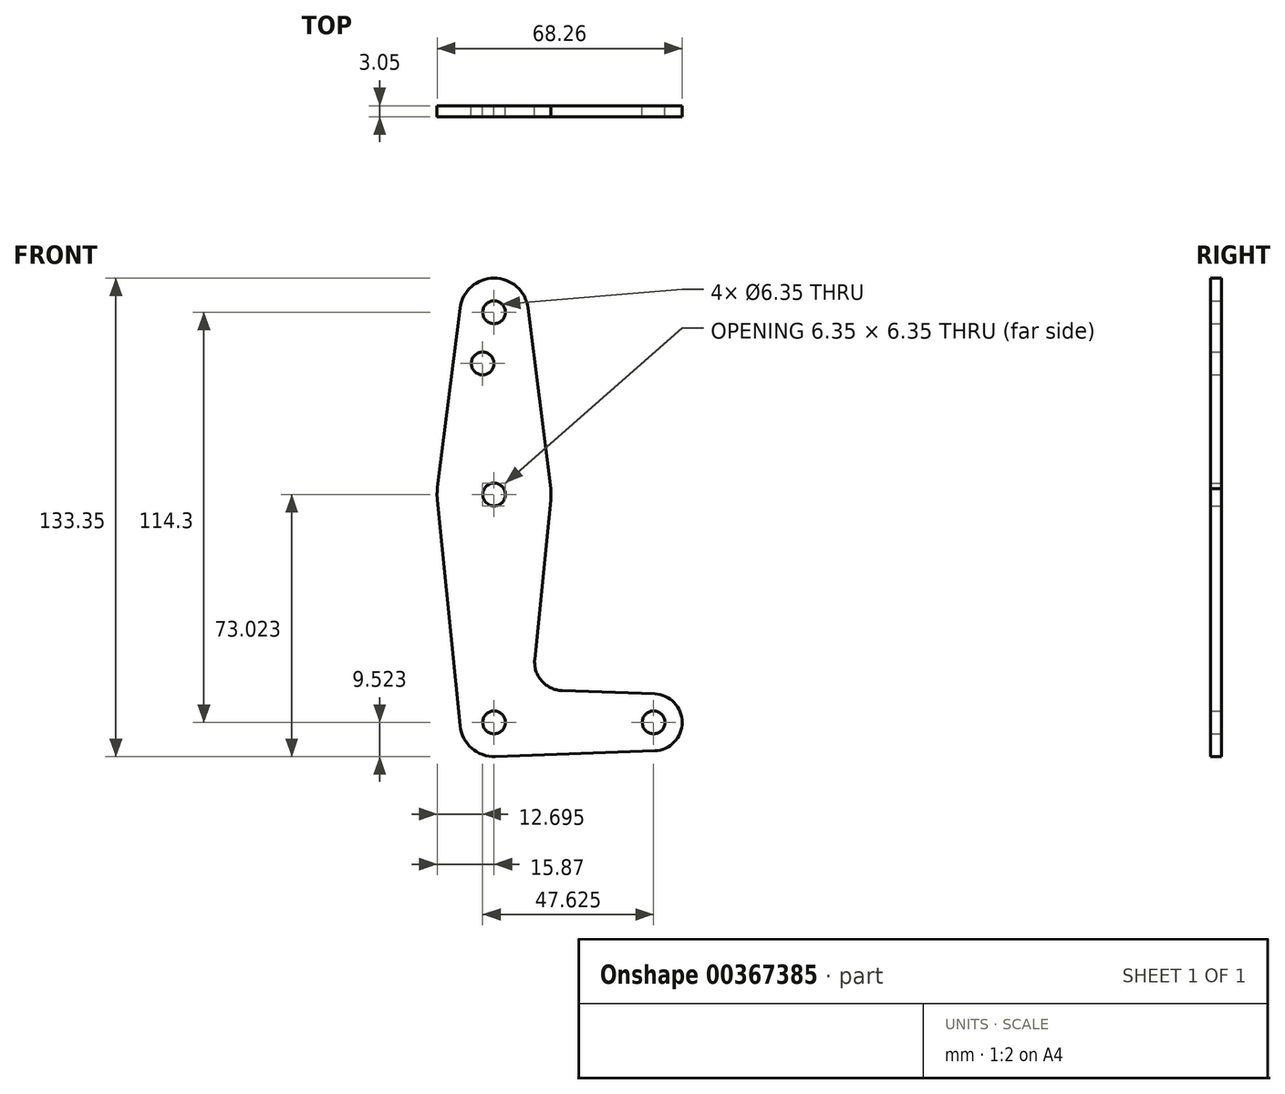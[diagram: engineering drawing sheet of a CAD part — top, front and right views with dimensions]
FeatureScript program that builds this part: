
annotation { "Feature Type Name" : "Feature", "Feature Type Description" : "" }
export const myFeature = defineFeature(function(context is Context, id is Id, definition is map)
    precondition{}
    {
        {
            var Q0;
            Q0=qCreatedBy(makeId("Front.planeOp"),FACE);
            var sketch = newSketch(context, id + "F0", { "sketchPlane" : qUnion([Q0])});
            skLineSegment(sketch, "E0", {"start": v(-44.45, -50.99) * mm, "end": v(-44.45, 63.31) * mm});
            skCircle(sketch, "E1", {"center": v(-44.45, 63.31) * mm, "radius": 9.53 * mm});
            skLineSegment(sketch, "E2", {"start": v(-44.45, -50.99) * mm, "end": v(0, -50.99) * mm});
            skCircle(sketch, "E3", {"center": v(0, -50.99) * mm, "radius": 7.94 * mm});
            skCircle(sketch, "E4", {"center": v(-44.45, -50.99) * mm, "radius": 9.53 * mm});
            skCircle(sketch, "E5", {"center": v(-44.45, 12.51) * mm, "radius": 15.88 * mm});
            skLineSegment(sketch, "E6", {"start": v(-53.9, 64.5) * mm, "end": v(-60.2, 14.5) * mm});
            skLineSegment(sketch, "E7", {"start": v(-53.93, -51.94) * mm, "end": v(-60.25, 10.93) * mm});
            skLineSegment(sketch, "E8", {"start": v(-33.1, -33.4) * mm, "end": v(-28.65, 10.93) * mm});
            skLineSegment(sketch, "E9", {"start": v(-28.65, 14.1) * mm, "end": v(-35, 64.5) * mm});
            skLineSegment(sketch, "E10", {"start": v(-25.48, -42.14) * mm, "end": v(0.28, -43.05) * mm});
            skLineSegment(sketch, "E11", {"start": v(0.28, -43.05) * mm, "end": v(0.28, -58.92) * mm});
            skLineSegment(sketch, "E12", {"start": v(0.28, -58.92) * mm, "end": v(-44.1, -60.5) * mm});
            skCircle(sketch, "E13", {"center": v(-44.45, 63.31) * mm, "radius": 3.18 * mm});
            skCircle(sketch, "E14", {"center": v(-47.62, 49.04) * mm, "radius": 3.18 * mm});
            skCircle(sketch, "E15", {"center": v(-44.45, 12.51) * mm, "radius": 3.18 * mm});
            skCircle(sketch, "E16", {"center": v(-44.45, -50.99) * mm, "radius": 3.18 * mm});
            skCircle(sketch, "E17", {"center": v(0, -50.99) * mm, "radius": 3.18 * mm});
            skArc(sketch, "E18.filletArc", {"start": v(-33.1, -33.4) * mm, "mid": v(-31.19, -39.42) * mm, "end": v(-25.48, -42.14) * mm});
            skSolve(sketch);
        }
        {
            var Q0;
            Q0=makeQuery(id+"F0.imprint","IMPRINT",FACE,{"disambiguationData":[TD([[makeQuery(id+"F0.imprint","IMPRINT",EDGE,{"derivedFrom":sQuery(id+"F0.wireOp",EDGE,"E13")}),-1.0]])]});
            var Q1;
            {var subQ3=sQuery(id+"F0.wireOp",EDGE,"E0");var subQ8=makeQuery(id+"F0.imprint","INTERSECT",VERTEX,{"derivedFrom":[subQ3,sQuery(id+"F0.wireOp",EDGE,"E14")]});Q1=makeQuery(id+"F0.imprint","IMPRINT",FACE,{"disambiguationData":[TD([[makeQuery(id+"F0.imprint","IMPRINT",EDGE,{"disambiguationData":[TD([[subQ8,1.0]])],"derivedFrom":subQ3}),-1.0]])]});}
            var Q2;
            {var subQ0=sQuery(id+"F0.wireOp",EDGE,"E6");Q2=makeQuery(id+"F0.imprint","IMPRINT",FACE,{"disambiguationData":[TD([[makeQuery(id+"F0.imprint","IMPRINT",EDGE,{"derivedFrom":subQ0}),1.0]])]});}
            var Q3;
            {var subQ0=sQuery(id+"F0.wireOp",EDGE,"E5");var subQ2=sQuery(id+"F0.wireOp",EDGE,"E0");var subQ5=makeQuery(id+"F0.imprint","INTERSECT",VERTEX,{"disambiguationData":[OD(0.0)],"derivedFrom":[subQ2,subQ0]});Q3=makeQuery(id+"F0.imprint","IMPRINT",FACE,{"disambiguationData":[TD([[makeQuery(id+"F0.imprint","IMPRINT",EDGE,{"disambiguationData":[TD([[subQ5,-1.0]])],"derivedFrom":subQ2}),1.0]])]});}
            var Q4;
            {var subQ0=sQuery(id+"F0.wireOp",EDGE,"E5");var subQ2=sQuery(id+"F0.wireOp",EDGE,"E0");var subQ3=makeQuery(id+"F0.imprint","INTERSECT",VERTEX,{"disambiguationData":[OD(0.0)],"derivedFrom":[subQ2,subQ0]});Q4=makeQuery(id+"F0.imprint","IMPRINT",FACE,{"disambiguationData":[TD([[makeQuery(id+"F0.imprint","IMPRINT",EDGE,{"disambiguationData":[TD([[subQ3,-1.0]])],"derivedFrom":subQ2}),-1.0]])]});}
            var Q5;
            {var subQ10=sQuery(id+"F0.wireOp",EDGE,"E8");Q5=makeQuery(id+"F0.imprint","IMPRINT",FACE,{"disambiguationData":[TD([[makeQuery(id+"F0.imprint","IMPRINT",EDGE,{"derivedFrom":subQ10}),1.0]])]});}
            var Q6;
            {var subQ5=sQuery(id+"F0.wireOp",EDGE,"E7");Q6=makeQuery(id+"F0.imprint","IMPRINT",FACE,{"disambiguationData":[TD([[makeQuery(id+"F0.imprint","IMPRINT",EDGE,{"derivedFrom":subQ5}),-1.0]])]});}
            var Q7;
            {var subQ5=sQuery(id+"F0.wireOp",EDGE,"E12");Q7=makeQuery(id+"F0.imprint","IMPRINT",FACE,{"disambiguationData":[TD([[makeQuery(id+"F0.imprint","IMPRINT",EDGE,{"derivedFrom":subQ5}),-1.0]])]});}
            var Q8;
            {var subQ3=sQuery(id+"F0.wireOp",EDGE,"E0");var subQ5=sQuery(id+"F0.wireOp",EDGE,"E16");var subQ9=makeQuery(id+"F0.imprint","INTERSECT",VERTEX,{"derivedFrom":[subQ3,subQ5]});Q8=makeQuery(id+"F0.imprint","IMPRINT",FACE,{"disambiguationData":[TD([[makeQuery(id+"F0.imprint","IMPRINT",EDGE,{"disambiguationData":[TD([[subQ9,-1.0]])],"derivedFrom":subQ3}),1.0]])]});}
            var Q9;
            {var subQ0=sQuery(id+"F0.wireOp",EDGE,"E16");var subQ1=sQuery(id+"F0.wireOp",EDGE,"E0");var subQ2=makeQuery(id+"F0.imprint","INTERSECT",VERTEX,{"derivedFrom":[subQ1,subQ0]});Q9=makeQuery(id+"F0.imprint","IMPRINT",FACE,{"disambiguationData":[TD([[makeQuery(id+"F0.imprint","IMPRINT",EDGE,{"disambiguationData":[TD([[subQ2,-1.0]])],"derivedFrom":subQ1}),-1.0]])]});}
            var Q10;
            {var subQ0=sQuery(id+"F0.wireOp",EDGE,"E11");var subQ4=sQuery(id+"F0.wireOp",EDGE,"E17");var subQ6=makeQuery(id+"F0.imprint","INTERSECT",VERTEX,{"disambiguationData":[OD(0.0)],"derivedFrom":[subQ0,subQ4]});Q10=makeQuery(id+"F0.imprint","IMPRINT",FACE,{"disambiguationData":[TD([[makeQuery(id+"F0.imprint","IMPRINT",EDGE,{"disambiguationData":[TD([[subQ6,1.0]])],"derivedFrom":subQ4}),-1.0]])]});}
            var Q11;
            {var subQ0=sQuery(id+"F0.wireOp",EDGE,"E17");var subQ1=sQuery(id+"F0.wireOp",EDGE,"E2");var subQ2=makeQuery(id+"F0.imprint","INTERSECT",VERTEX,{"derivedFrom":[subQ1,subQ0]});Q11=makeQuery(id+"F0.imprint","IMPRINT",FACE,{"disambiguationData":[TD([[makeQuery(id+"F0.imprint","IMPRINT",EDGE,{"disambiguationData":[TD([[subQ2,1.0]])],"derivedFrom":subQ1}),1.0]])]});}
            var Q12;
            {var subQ0=sQuery(id+"F0.wireOp",EDGE,"E17");var subQ1=sQuery(id+"F0.wireOp",EDGE,"E2");var subQ2=makeQuery(id+"F0.imprint","INTERSECT",VERTEX,{"derivedFrom":[subQ1,subQ0]});Q12=makeQuery(id+"F0.imprint","IMPRINT",FACE,{"disambiguationData":[TD([[makeQuery(id+"F0.imprint","IMPRINT",EDGE,{"disambiguationData":[TD([[subQ2,1.0]])],"derivedFrom":subQ1}),-1.0]])]});}
            extrude(context, id + "F1", {"entities" : qUnion([Q0, Q1, Q2, Q3, Q4, Q5, Q6, Q7, Q8, Q9, Q10, Q11, Q12]), "depth" : 3.05 * mm});
        }
    });
